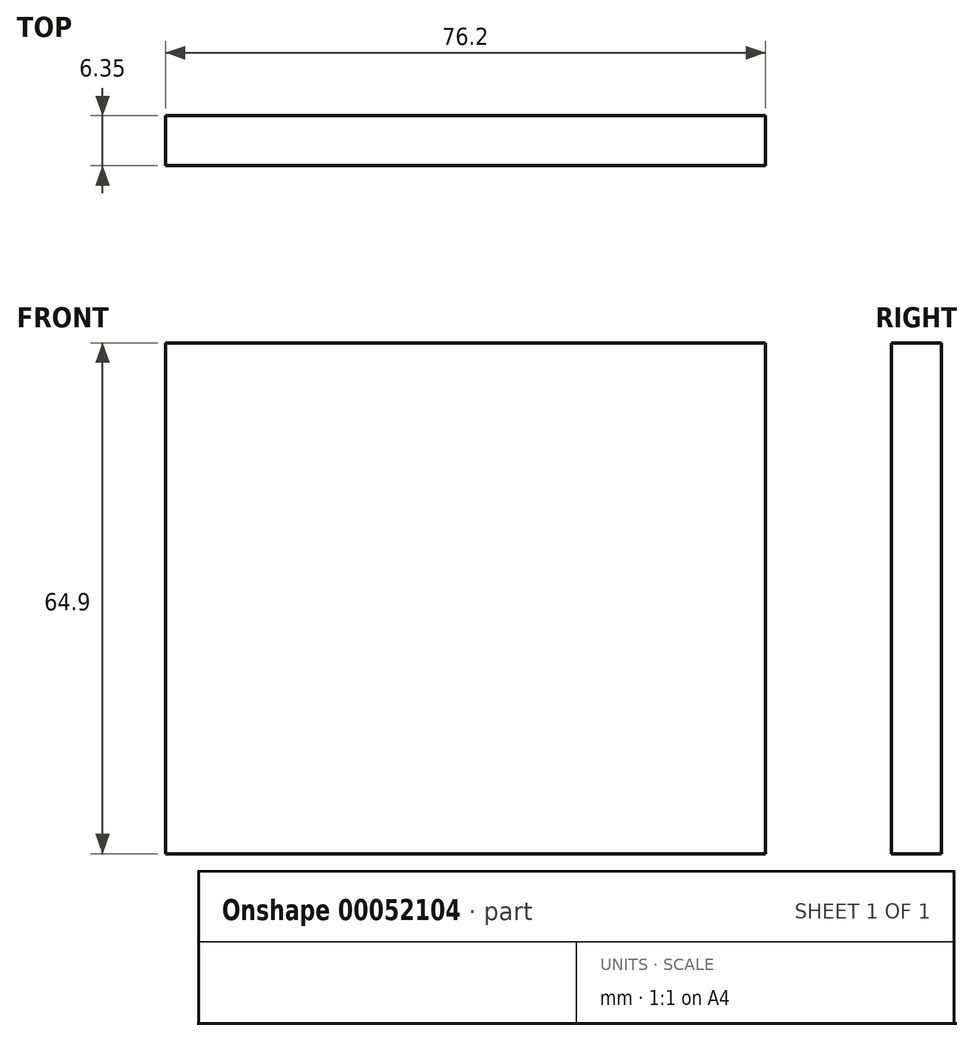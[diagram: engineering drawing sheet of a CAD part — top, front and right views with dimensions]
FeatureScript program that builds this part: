
annotation { "Feature Type Name" : "Feature", "Feature Type Description" : "" }
export const myFeature = defineFeature(function(context is Context, id is Id, definition is map)
    precondition{}
    {
        {
            var Q0;
            Q0=qCreatedBy(makeId("Front.planeOp"),FACE);
            var sketch = newSketch(context, id + "F0", { "sketchPlane" : qUnion([Q0])});
            skLineSegment(sketch, "E0.rect.bottom", {"start": v(-38.1, 32.45) * mm, "end": v(38.1, 32.45) * mm});
            skLineSegment(sketch, "E0.rect.top", {"start": v(-38.1, -32.45) * mm, "end": v(38.1, -32.45) * mm});
            skLineSegment(sketch, "E0.rect.left", {"start": v(-38.1, 32.45) * mm, "end": v(-38.1, -32.45) * mm});
            skLineSegment(sketch, "E0.rect.right", {"start": v(38.1, 32.45) * mm, "end": v(38.1, -32.45) * mm});
            skPoint(sketch, "E0.rect.middle", {"position": v(0, 0) * mm});
            skSolve(sketch);
        }
        {
            var Q0;
            Q0 = qSketchRegion(id + "F0", true);
            extrude(context, id + "F1", {"entities" : qUnion([Q0]), "depth" : 6.35 * mm});
        }
    });
